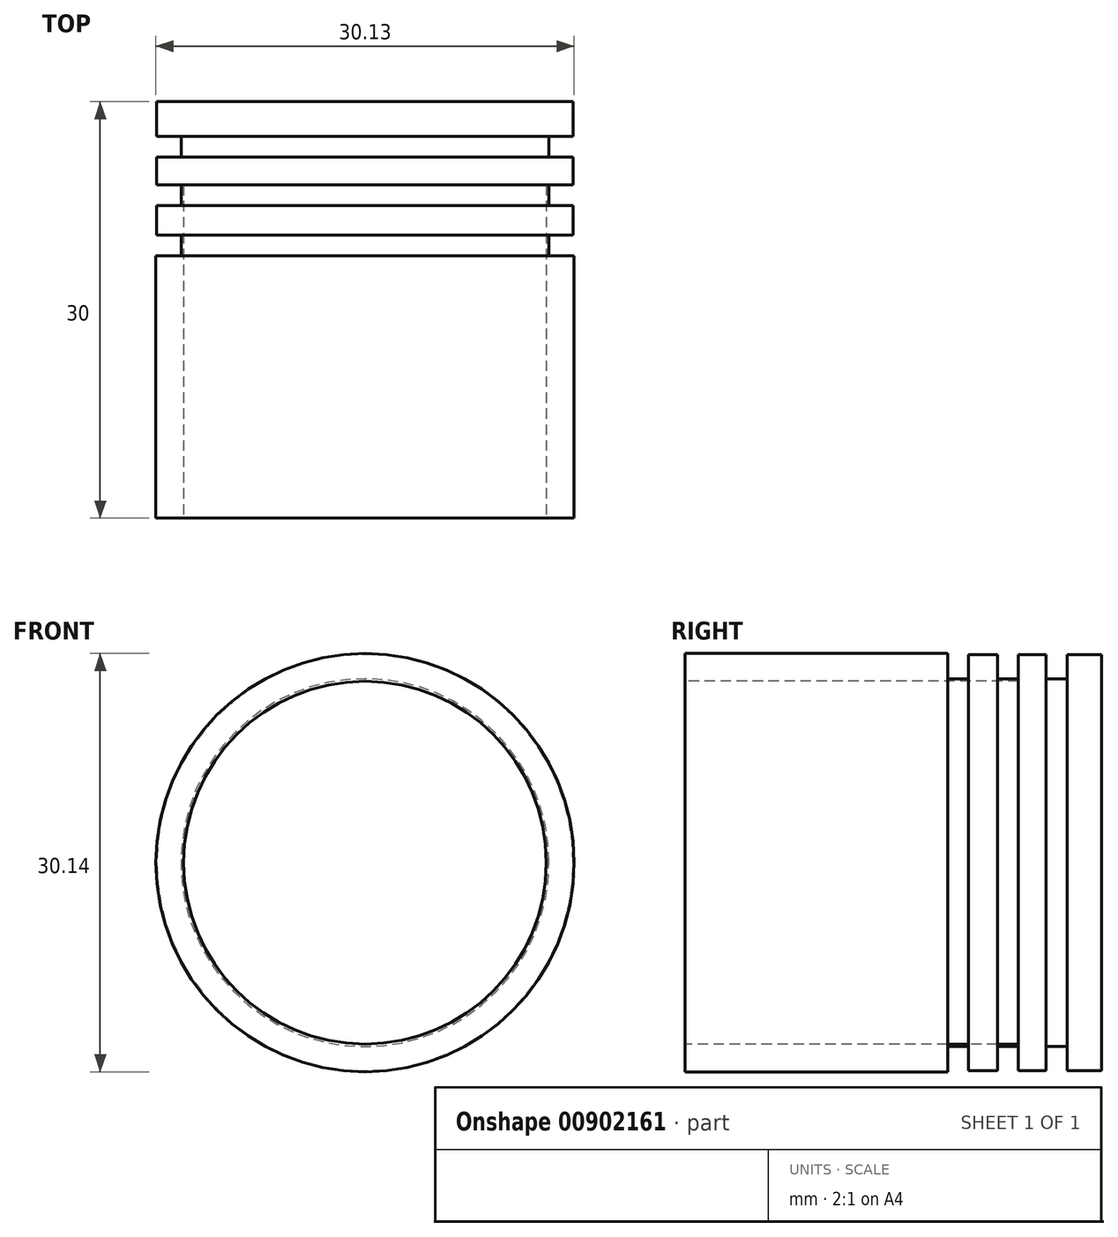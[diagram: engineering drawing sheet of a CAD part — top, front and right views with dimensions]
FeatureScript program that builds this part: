
annotation { "Feature Type Name" : "Feature", "Feature Type Description" : "" }
export const myFeature = defineFeature(function(context is Context, id is Id, definition is map)
    precondition{}
    {
        {
            var Q0;
            Q0=qCreatedBy(makeId("Top.planeOp"),FACE);
            var sketch = newSketch(context, id + "F0", { "sketchPlane" : qUnion([Q0])});
            skLineSegment(sketch, "E0.MirrorCS", {"start": v(-17.21, 22.28) * mm, "end": v(-17.21, 20.18) * mm});
            skLineSegment(sketch, "E1.MirrorCS", {"start": v(-18.96, 20.18) * mm, "end": v(-18.96, 18.68) * mm});
            skLineSegment(sketch, "E2.MirrorCS", {"start": v(-17.15, 18.68) * mm, "end": v(-17.15, 16.68) * mm});
            skLineSegment(sketch, "E3.MirrorCS", {"start": v(-17.15, 4.52) * mm, "end": v(-17.15, -0.22) * mm});
            skLineSegment(sketch, "E4.MirrorCS", {"start": v(-17.21, 27.28) * mm, "end": v(-17.21, 29.78) * mm});
            skLineSegment(sketch, "E5.MirrorCS", {"start": v(-17.21, 25.78) * mm, "end": v(-17.21, 23.78) * mm});
            skLineSegment(sketch, "E6", {"start": v(-17.15, 18.68) * mm, "end": v(-32.21, 18.68) * mm});
            skLineSegment(sketch, "E7", {"start": v(-17.21, 20.18) * mm, "end": v(-32.21, 20.18) * mm});
            skLineSegment(sketch, "E8", {"start": v(-17.21, 22.28) * mm, "end": v(-32.21, 22.28) * mm});
            skLineSegment(sketch, "E9", {"start": v(-17.21, 23.78) * mm, "end": v(-32.21, 23.78) * mm});
            skLineSegment(sketch, "E10", {"start": v(-17.21, 25.78) * mm, "end": v(-32.21, 25.78) * mm});
            skLineSegment(sketch, "E11", {"start": v(-17.21, 27.28) * mm, "end": v(-32.21, 27.28) * mm});
            skLineSegment(sketch, "E12", {"start": v(-17.21, 29.78) * mm, "end": v(-32.21, 29.78) * mm});
            skLineSegment(sketch, "E13", {"start": v(-17.15, 16.68) * mm, "end": v(-17.15, 4.52) * mm});
            skLineSegment(sketch, "E14", {"start": v(-17.15, 16.68) * mm, "end": v(-20.65, 16.68) * mm});
            skLineSegment(sketch, "E15", {"start": v(-20.65, 16.68) * mm, "end": v(-20.65, 17.38) * mm});
            skLineSegment(sketch, "E16", {"start": v(-20.65, 17.38) * mm, "end": v(-21.65, 17.38) * mm});
            skLineSegment(sketch, "E17", {"start": v(-21.65, 17.38) * mm, "end": v(-21.65, 16.68) * mm});
            skLineSegment(sketch, "E18", {"start": v(-21.65, 16.68) * mm, "end": v(-25.85, 16.68) * mm});
            skLineSegment(sketch, "E19", {"start": v(-25.85, 16.68) * mm, "end": v(-32.21, 16.68) * mm});
            skLineSegment(sketch, "E20", {"start": v(-18.96, 22.28) * mm, "end": v(-18.96, 23.78) * mm});
            skLineSegment(sketch, "E21", {"start": v(-18.96, 25.78) * mm, "end": v(-18.96, 27.28) * mm});
            skLineSegment(sketch, "E22", {"start": v(-32.21, 1.53) * mm, "end": v(-32.21, 29.78) * mm});
            skLineSegment(sketch, "E23", {"start": v(-17.15, -0.22) * mm, "end": v(-19.15, -0.22) * mm});
            skLineSegment(sketch, "E24", {"start": v(-19.15, -0.22) * mm, "end": v(-19.15, 1.53) * mm});
            skLineSegment(sketch, "E25", {"start": v(-32.21, 1.53) * mm, "end": v(-19.15, 1.53) * mm});
            skLineSegment(sketch, "E26", {"start": v(-32.21, 1.53) * mm, "end": v(-32.21, 9.13) * mm});
            skLineSegment(sketch, "E27", {"start": v(-17.15, 9.32) * mm, "end": v(-17.15, 16.68) * mm});
            skSolve(sketch);
        }
        {
            var Q0;
            Q0=makeQuery(id+"F0.imprint","IMPRINT",FACE,{"disambiguationData":[TD([[makeQuery(id+"F0.imprint","IMPRINT",EDGE,{"derivedFrom":sQuery(id+"F0.wireOp",EDGE,"E3.MirrorCS")}),-1.0]])]});
            var Q1;
            {var subQ2=sQuery(id+"F0.wireOp",EDGE,"E2.MirrorCS");Q1=makeQuery(id+"F0.imprint","IMPRINT",FACE,{"disambiguationData":[TD([[makeQuery(id+"F0.imprint","IMPRINT",EDGE,{"derivedFrom":subQ2}),-1.0]])]});}
            var Q2;
            {var subQ6=sQuery(id+"F0.wireOp",EDGE,"E0.MirrorCS");Q2=makeQuery(id+"F0.imprint","IMPRINT",FACE,{"disambiguationData":[TD([[makeQuery(id+"F0.imprint","IMPRINT",EDGE,{"derivedFrom":subQ6}),-1.0]])]});}
            var Q3;
            {var subQ0=sQuery(id+"F0.wireOp",EDGE,"E1.MirrorCS");Q3=makeQuery(id+"F0.imprint","IMPRINT",FACE,{"disambiguationData":[TD([[makeQuery(id+"F0.imprint","IMPRINT",EDGE,{"derivedFrom":subQ0}),-1.0]])]});}
            var Q4;
            {var subQ3=sQuery(id+"F0.wireOp",EDGE,"E20");Q4=makeQuery(id+"F0.imprint","IMPRINT",FACE,{"disambiguationData":[TD([[makeQuery(id+"F0.imprint","IMPRINT",EDGE,{"derivedFrom":subQ3}),1.0]])]});}
            var Q5;
            {var subQ1=sQuery(id+"F0.wireOp",EDGE,"E5.MirrorCS");Q5=makeQuery(id+"F0.imprint","IMPRINT",FACE,{"disambiguationData":[TD([[makeQuery(id+"F0.imprint","IMPRINT",EDGE,{"derivedFrom":subQ1}),-1.0]])]});}
            var Q6;
            {var subQ3=sQuery(id+"F0.wireOp",EDGE,"E21");Q6=makeQuery(id+"F0.imprint","IMPRINT",FACE,{"disambiguationData":[TD([[makeQuery(id+"F0.imprint","IMPRINT",EDGE,{"derivedFrom":subQ3}),1.0]])]});}
            var Q7;
            {var subQ5=sQuery(id+"F0.wireOp",EDGE,"E4.MirrorCS");Q7=makeQuery(id+"F0.imprint","IMPRINT",FACE,{"disambiguationData":[TD([[makeQuery(id+"F0.imprint","IMPRINT",EDGE,{"derivedFrom":subQ5}),1.0]])]});}
            var Q8;
            Q8=sQuery(id+"F0.wireOp",EDGE,"E22");
            revolve(context, id + "F1", {"surfaceOperationType" : NewSurfaceOperationType.NEW, "entities" : qUnion([Q0, Q1, Q2, Q3, Q4, Q5, Q6, Q7]), "axis" : qUnion([Q8]), "revolveType" : RevolveType.FULL});
        }
        {
            var Q0;
            Q0=makeQuery(id+"F1.opRevolve","SWEPT_FACE",FACE,{"disambiguationData":[OSD([sQuery(id+"F0.wireOp",EDGE,"E25")])]});
            extrude(context, id + "F2", {"entities" : qUnion([Q0]), "operationType" : NewBodyOperationType.REMOVE, "oppositeDirection" : true, "depth" : 22.25 * mm, "offsetDistance" : 25 * mm});
        }
    });
